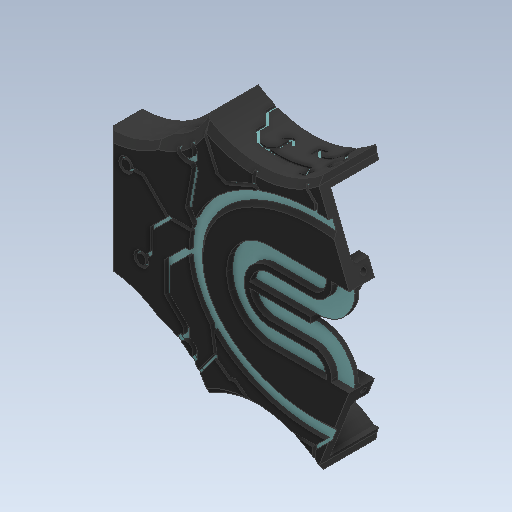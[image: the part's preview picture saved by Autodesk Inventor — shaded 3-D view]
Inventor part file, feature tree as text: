
AUTODESK INVENTOR PART (.ipt)
format: ipt  version: 2020 (Build 240168000, 168)  size: 1,960,448 bytes
history: native  units: mm
features: reference x74, projected_geometry x25, sketch x18, extrude x17, plane x6, other x6, fillet x5, chamfer x5, mirror x2, emboss x2
ambient origin geometry x8: Origin, YZ Plane, XZ Plane, XY Plane, X Axis, Y Axis, Z Axis, Center Point
bodies: Solid1 (feature_tree)
feature tree (160):
  extrude  "Extrusion1"  Depth=70.0mm
  extrude  "Extrusion4"  Depth=29.189217mm
  extrude  "Extrusion7"  Depth=20.0mm TaperAngle=0.0deg
  extrude  "Extrusion8"  Depth=36.552mm TaperAngle=0.0deg
  extrude  "Extrusion9"  Depth=20.0mm
  plane  "Work Plane2"
  mirror  "Mirror1"
  extrude  "Extrusion10"  Depth=26.0mm
  fillet  "Fillet3"  Radius=15.25mm
  fillet  "Fillet4"  Radius=35.5mm
  plane  "Work Plane3"
  extrude  "Extrusion11"  Depth=26.5mm TaperAngle=0.0deg
  plane  "Work Plane4"
  extrude  "Extrusion12"  Depth=46.75mm
  plane  "Work Plane5"
  extrude  "Extrusion14"  Depth=1.6mm TaperAngle=0.0deg
  fillet  "Fillet5"  Radius=78.75mm
  fillet  "Fillet6"  Radius=3.0mm
  fillet  "Fillet8"  Radius=8.0mm
  extrude  "Extrusion15"  Depth=8.0mm TaperAngle=0.0deg
  plane  "Work Plane6"
  extrude  "Extrusion17"  Depth=8.0mm
  emboss  "Emboss1"
  chamfer  "Chamfer3"  Distance=2.0mm
  chamfer  "Chamfer4"  Distance=10.0mm
  extrude  "Extrusion18"  Depth=2.0mm TaperAngle=45.0deg
  extrude  "Extrusion19"  Depth=2.0mm
  extrude  "Extrusion22"  Depth=45.0mm
  extrude  "Extrusion23"  Depth=60.0mm
  chamfer  "Chamfer5"  Distance=65.0mm
  extrude  "Extrusion24"  Depth=50.0mm
  extrude  "Extrusion25"  Depth=2.0mm TaperAngle=0.0deg
  chamfer  "Chamfer8"  Angle=135.0deg  [1 undecoded]
  plane  "Work Plane8"
  emboss  "Emboss4"
  mirror  "Mirror2"
  chamfer  "Chamfer9"  Distance=1.5mm
  sketch  "Sketch1"  dims[d0=10.0mm d1=0.0mm d6=70.0mm]
  reference  "Reference1"
  reference  "Reference2"
  reference  "Reference3"
  reference  "Reference4"
  reference  "Reference5"
  reference  "Reference6"
  reference  "Reference7"
  reference  "Reference8"
  reference  "Reference9"
  reference  "Reference10"
  reference  "Reference11"
  reference  "Reference12"
  reference  "Reference13"
  reference  "Reference14"
  reference  "Reference15"
  reference  "Reference16"
  reference  "Reference17"
  reference  "Reference18"
  reference  "Reference19"
  reference  "Reference20"
  reference  "Reference21"
  reference  "Reference22"
  reference  "Reference23"
  reference  "Reference24"
  reference  "Reference25"
  reference  "Reference26"
  reference  "Reference27"
  reference  "Reference28"
  reference  "Reference29"
  reference  "Reference30"
  reference  "Reference31"
  reference  "Reference32"
  reference  "Reference33"
  reference  "Reference34"
  reference  "Reference35"
  reference  "Reference36"
  reference  "Reference37"
  reference  "Reference38"
  reference  "Reference39"
  reference  "Reference40"
  reference  "Reference41"
  reference  "Reference42"
  reference  "Reference43"
  reference  "Reference44"
  reference  "Reference45"
  reference  "Reference46"
  reference  "Reference47"
  reference  "Reference48"
  reference  "Reference49"
  reference  "Reference50"
  reference  "Reference51"
  reference  "Reference52"
  reference  "Reference53"
  reference  "Reference54"
  reference  "Reference55"
  reference  "Reference56"
  reference  "Reference57"
  reference  "Reference58"
  reference  "Reference59"
  reference  "Reference60"
  reference  "Reference61"
  reference  "Reference62"
  sketch  "Sketch5"  dims[d7=29.189217mm d8=29.189217mm]
  sketch  "Sketch8"  dims[d9=5.0mm d10=0.0mm d21=20.0mm d22=0.0mm]
  projected_geometry  "Projected Loop39"
  sketch  "Sketch9"  dims[d23=4.0mm d24=0.0mm d25=36.552mm d26=0.0mm]
  reference  "Reference110"
  projected_geometry  "Projected Loop40"
  sketch  "Sketch10"  dims[d27=10.0mm d28=20.0mm]
  projected_geometry  "Projected Loop41"
  sketch  "Sketch11"  dims[d29=20.0mm d30=0.0mm d31=26.0mm d32=15.25mm d33=35.5mm d34=0.0mm]
  projected_geometry  "Projected Loop42"
  sketch  "Sketch12"  dims[d35=5.0mm d36=0.0mm d39=26.5mm d40=0.0mm]
  reference  "Reference111"
  reference  "Reference112"
  reference  "Reference113"
  sketch  "Sketch14"  dims[d41=26.0mm d42=46.75mm]
  projected_geometry  "Projected Loop43"
  projected_geometry  "Projected Loop44"
  sketch  "Sketch16"  dims[d44=5.0mm d45=1.6mm d46=0.0mm d250=78.75mm d251=0.0mm d253=3.0mm d254=0.0mm]
  sketch  "Sketch17"  dims[d255=3.0mm d256=2.0mm d257=45.0deg]
  reference  "Reference114"
  reference  "Reference115"
  reference  "Reference116"
  reference  "Reference117"
  reference  "Reference118"
  reference  "Reference119"
  reference  "Reference120"
  reference  "Reference121"
  sketch  "Sketch19"  dims[d258=5.0mm d259=2.0mm d260=45.0deg]
  sketch  "Sketch22"  dims[d261=10.0mm d262=63.75mm d263=0.0mm d264=0.0mm d265=8.0mm]
  sketch  "Sketch23"  dims[d266=8.0mm d267=8.0mm d268=0.0mm]
  projected_geometry  "Projected Loop51"
  projected_geometry  "Projected Loop52"
  projected_geometry  "Projected Loop53"
  projected_geometry  "Projected Loop54"
  projected_geometry  "Projected Loop55"
  projected_geometry  "Projected Loop56"
  projected_geometry  "Projected Loop57"
  projected_geometry  "Projected Loop58"
  projected_geometry  "Projected Loop59"
  projected_geometry  "Projected Loop60"
  projected_geometry  "Projected Loop61"
  projected_geometry  "Projected Loop62"
  sketch  "Sketch27"  dims[d279=8.0mm d280=8.0mm]
  projected_geometry  "Projected Loop67"
  projected_geometry  "Projected Loop68"
  sketch  "Sketch28"  dims[d281=7.0mm]
  projected_geometry  "Projected Loop69"
  projected_geometry  "Projected Loop70"
  sketch  "Sketch29"  dims[d282=7.0mm d283=2.0mm d284=0.0mm]
  projected_geometry  "Projected Loop71"
  sketch  "Sketch30"  dims[d285=3.0mm]
  projected_geometry  "Projected Loop72"
  sketch  "Sketch32"  dims[d286=3.0mm d287=10.0mm d288=0.0mm d289=2.0mm d290=2.0mm d291=45.0deg d292=2.0mm d293=45.0mm d294=60.0mm d295=65.0mm d296=50.0mm d297=2.0mm d298=0.0mm d299=135.0deg d300=1.5mm d301=135.0deg d302=2.5mm d303=7.0mm d304=7.0mm d305=2.5mm d306=1.5mm d307=1.5mm d308=135.0deg d309=135.0deg d310=135.0deg d311=135.0deg d312=135.0deg d313=1.5mm d314=1.5mm d315=135.0deg d316=1.5mm d317=1.5mm d318=135.0deg d319=135.0deg d320=90.0deg d321=135.0deg d322=135.0deg d323=135.0deg d324=135.0deg d325=135.0deg d326=1.5mm d327=1.5mm d328=5.0mm d329=1.25mm d330=5.0mm d331=1.25mm d332=1.5mm d333=135.0deg d334=135.0deg d335=90.0deg d336=1.5mm d337=90.0deg d338=1.5mm d339=15.445915mm d340=5.594061mm d341=2.322946mm d342=29.639109mm d343=20.473175mm d344=105.653831mm d345=104.832781mm d346=73.870631mm d347=72.108228mm d348=6.550189mm d349=77.436747mm d350=84.208796mm d351=112.825073mm d352=51.891468mm d353=13.848735mm d354=7.830864mm d355=20.909441mm d356=120.259435mm d357=147.543087mm d358=215.899904mm d359=119.257097mm d360=217.912257mm d361=118.363121mm d362=196.092916mm d363=173.474061mm d364=64.203809mm d365=230.008807mm d366=88.455475mm d367=38.738257mm d368=6.782198mm d369=49.177714mm d370=7.893801mm d371=53.028323mm d372=36.454973mm d373=37.87355mm d374=36.376863mm d375=76.62551mm d376=89.596763mm d377=86.006538mm d378=57.824736mm d379=100.296308mm d380=76.330699mm d381=79.250121mm d382=81.646395mm d383=102.089905mm d384=85.494365mm d385=86.598543mm d386=69.08423mm d387=72.003652mm d388=104.879312mm d389=92.658856mm d390=39.207502mm d391=2.0mm d392=0.0mm d399=2.0mm d400=2.0mm d401=45.0deg d402=8.184773mm d403=5.0mm d404=9.195572mm d405=1.5mm d406=135.0deg d407=135.0deg d408=6.0mm d409=5.0mm d410=135.0deg d411=1.5mm d412=3.0mm d414=1.5mm d415=3.0mm d416=4.0mm d417=2.0mm d418=135.0deg d419=1.5mm d420=1.5mm d421=135.0deg d422=3.5mm d423=1.5mm d424=1.5mm d425=6.0mm d426=6.0mm d427=3.5mm d428=135.0deg d429=1.5mm d430=90.0deg d431=90.0deg d434=4.0mm d436=2.0mm d437=45.0deg d438=1.5mm d439=1.5mm d440=135.0deg d441=3.5mm d442=3.5mm d443=135.0deg d447=1.5mm d449=2.0mm d450=45.0deg d451=15.707962mm d452=90.0deg d453=135.0deg d455=1.5mm d456=90.0deg d457=6.0mm d458=4.0mm d459=135.0deg d460=1.5mm d461=135.0deg d462=1.5mm d463=1.5mm d464=90.0deg d465=2.0mm d466=45.0deg d467=2.0mm d468=1.5mm d469=3.5mm d470=1.5mm d471=90.0deg d474=2.0mm d475=1.5mm d476=1.0mm d477=0.0mm d478=2.0mm d479=2.0mm d480=45.0deg d2=0.5mm d3=0.872665mm d4=0.5mm d5=0.872665mm]
  projected_geometry  "Projected Loop73"
  parser-record x2  (decoder bookkeeping rows leaked as tree rows — omitted from the tree; the rows remain in map.json)
  other  "Assembly1.iam"
  other  "BodyTest2:1"
  other  "BodyBot:1"
  other  "BodyMid:1"
note: 1 required parameter value undecoded (feature->parameter linkage not recoverable at this tier; creation-order binding heuristic only, values carry confidence <= 0.55)
note: 2 file-system paths scrubbed to <path> (originals preserved in map.json)
